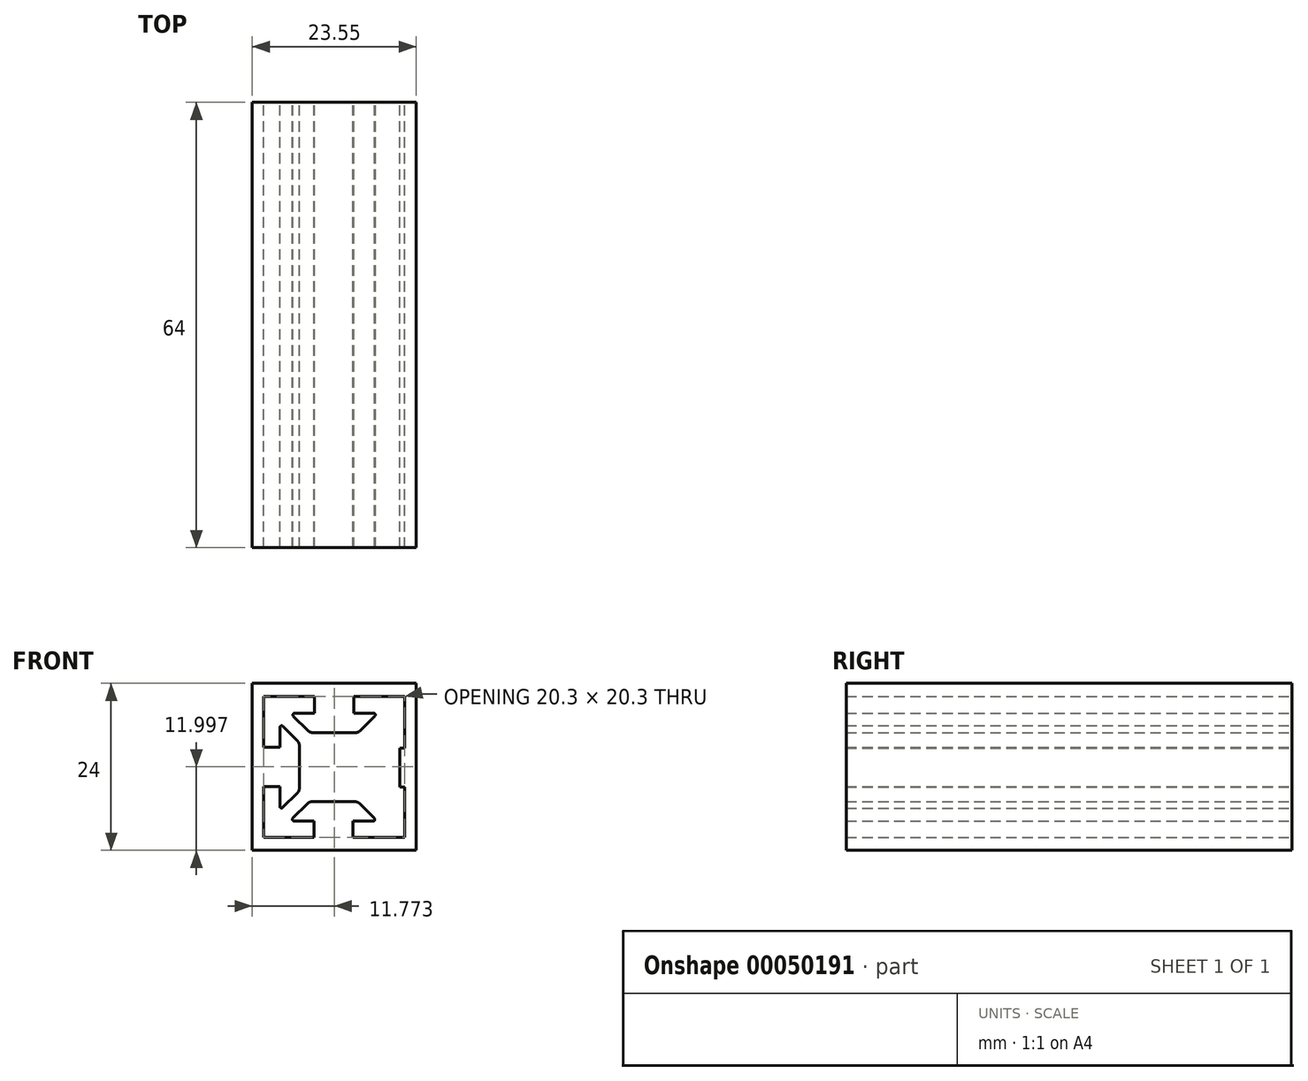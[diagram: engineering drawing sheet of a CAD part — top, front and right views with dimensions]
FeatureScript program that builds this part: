
annotation { "Feature Type Name" : "Feature", "Feature Type Description" : "" }
export const myFeature = defineFeature(function(context is Context, id is Id, definition is map)
    precondition{}
    {
        {
            var Q0;
            Q0=qCreatedBy(makeId("Front.planeOp"),FACE);
            var sketch = newSketch(context, id + "F0", { "sketchPlane" : qUnion([Q0])});
            skLineSegment(sketch, "E0", {"start": v(10.04, -9.96) * mm, "end": v(10.04, -2.96) * mm, "construction": true});
            skLineSegment(sketch, "E1", {"start": v(10.04, 3.04) * mm, "end": v(10.04, 10.04) * mm, "construction": true});
            skLineSegment(sketch, "E2", {"start": v(-6.7, -7.96) * mm, "end": v(-2.7, -3.96) * mm, "construction": true});
            skLineSegment(sketch, "E3", {"start": v(4.04, -2.63) * mm, "end": v(4.04, 2.78) * mm, "construction": true});
            skLineSegment(sketch, "E4", {"start": v(-2.7, -3.96) * mm, "end": v(2.91, -3.96) * mm, "construction": true});
            skLineSegment(sketch, "E5", {"start": v(2.91, -3.96) * mm, "end": v(6.91, -7.96) * mm, "construction": true});
            skLineSegment(sketch, "E6", {"start": v(-2.96, 10.04) * mm, "end": v(-9.96, 10.04) * mm, "construction": true});
            skLineSegment(sketch, "E7", {"start": v(-9.96, 10.04) * mm, "end": v(-9.96, 3.04) * mm, "construction": true});
            skCircle(sketch, "E8", {"center": v(0.04, 0.04) * mm, "radius": 2.1 * mm, "construction": true});
            skLineSegment(sketch, "E9", {"start": v(-7.96, 3.04) * mm, "end": v(-7.96, 6.79) * mm, "construction": true});
            skLineSegment(sketch, "E10", {"start": v(-7.96, 6.79) * mm, "end": v(-3.96, 2.79) * mm, "construction": true});
            skLineSegment(sketch, "E11", {"start": v(-3.96, 2.79) * mm, "end": v(-3.96, -2.71) * mm, "construction": true});
            skLineSegment(sketch, "E12", {"start": v(-3.96, -2.71) * mm, "end": v(-7.96, -6.71) * mm, "construction": true});
            skLineSegment(sketch, "E13", {"start": v(2.9, 4.04) * mm, "end": v(-2.7, 4.04) * mm, "construction": true});
            skLineSegment(sketch, "E14", {"start": v(6.91, -7.96) * mm, "end": v(3.04, -7.96) * mm, "construction": true});
            skLineSegment(sketch, "E15", {"start": v(-7.96, -6.71) * mm, "end": v(-7.96, -2.96) * mm, "construction": true});
            skLineSegment(sketch, "E16", {"start": v(-9.96, -2.96) * mm, "end": v(-9.96, -9.96) * mm, "construction": true});
            skLineSegment(sketch, "E17", {"start": v(-9.96, -9.96) * mm, "end": v(-2.96, -9.96) * mm, "construction": true});
            skLineSegment(sketch, "E18", {"start": v(-2.96, -7.96) * mm, "end": v(-6.7, -7.96) * mm, "construction": true});
            skLineSegment(sketch, "E19", {"start": v(10.04, 10.04) * mm, "end": v(3.04, 10.04) * mm, "construction": true});
            skLineSegment(sketch, "E20", {"start": v(4.04, 2.78) * mm, "end": v(8.04, 6.78) * mm, "construction": true});
            skLineSegment(sketch, "E21", {"start": v(3.04, 8.04) * mm, "end": v(6.91, 8.04) * mm, "construction": true});
            skLineSegment(sketch, "E22", {"start": v(8.04, -2.96) * mm, "end": v(8.04, -6.63) * mm, "construction": true});
            skLineSegment(sketch, "E23", {"start": v(-2.7, 4.04) * mm, "end": v(-6.7, 8.04) * mm, "construction": true});
            skLineSegment(sketch, "E24", {"start": v(8.04, 6.78) * mm, "end": v(8.04, 3.04) * mm, "construction": true});
            skLineSegment(sketch, "E25", {"start": v(6.91, 8.04) * mm, "end": v(2.9, 4.04) * mm, "construction": true});
            skLineSegment(sketch, "E26", {"start": v(8.04, -6.63) * mm, "end": v(4.04, -2.63) * mm, "construction": true});
            skLineSegment(sketch, "E27", {"start": v(-6.7, 8.04) * mm, "end": v(-2.96, 8.04) * mm, "construction": true});
            skLineSegment(sketch, "E28", {"start": v(3.04, -9.96) * mm, "end": v(10.04, -9.96) * mm, "construction": true});
            skLineSegment(sketch, "E29", {"start": v(8.04, 3.04) * mm, "end": v(10.04, 3.04) * mm, "construction": true});
            skLineSegment(sketch, "E30", {"start": v(-2.96, 8.04) * mm, "end": v(-2.96, 10.04) * mm, "construction": true});
            skLineSegment(sketch, "E31", {"start": v(-9.96, 3.04) * mm, "end": v(-7.96, 3.04) * mm, "construction": true});
            skLineSegment(sketch, "E32", {"start": v(3.04, 10.04) * mm, "end": v(3.04, 8.04) * mm, "construction": true});
            skLineSegment(sketch, "E33", {"start": v(10.04, -2.96) * mm, "end": v(8.04, -2.96) * mm, "construction": true});
            skLineSegment(sketch, "E34", {"start": v(-7.96, -2.96) * mm, "end": v(-9.96, -2.96) * mm, "construction": true});
            skLineSegment(sketch, "E35", {"start": v(-2.96, -9.96) * mm, "end": v(-2.96, -7.96) * mm, "construction": true});
            skLineSegment(sketch, "E36", {"start": v(3.04, -7.96) * mm, "end": v(3.04, -9.96) * mm, "construction": true});
            skLineSegment(sketch, "E37.0", {"start": v(-7.33, 5.88) * mm, "end": v(-5.25, 3.8) * mm});
            skLineSegment(sketch, "E38.0", {"start": v(-5.25, -3.72) * mm, "end": v(-7.33, -5.8) * mm});
            skLineSegment(sketch, "E39", {"start": v(-4.96, 3.09) * mm, "end": v(-4.96, -3.02) * mm});
            skLineSegment(sketch, "E40", {"start": v(-7.76, -5.63) * mm, "end": v(-7.76, -2.76) * mm});
            skLineSegment(sketch, "E41", {"start": v(-7.76, 5.7) * mm, "end": v(-7.76, 2.84) * mm});
            skPoint(sketch, "E42.visualSharp", {"position": v(-7.76, 6.3) * mm});
            skArc(sketch, "E42.filletArc", {"start": v(-7.33, 5.88) * mm, "mid": v(-7.6, 5.93) * mm, "end": v(-7.76, 5.7) * mm});
            skPoint(sketch, "E43.visualSharp", {"position": v(-7.76, -6.23) * mm});
            skArc(sketch, "E43.filletArc", {"start": v(-7.76, -5.63) * mm, "mid": v(-7.6, -5.86) * mm, "end": v(-7.33, -5.8) * mm});
            skPoint(sketch, "E44.visualSharp", {"position": v(-4.96, 3.5) * mm});
            skArc(sketch, "E44.filletArc", {"start": v(-4.96, 3.09) * mm, "mid": v(-5.03, 3.47) * mm, "end": v(-5.25, 3.8) * mm});
            skPoint(sketch, "E45.visualSharp", {"position": v(-4.96, -3.43) * mm});
            skArc(sketch, "E45.filletArc", {"start": v(-5.25, -3.72) * mm, "mid": v(-5.03, -3.4) * mm, "end": v(-4.96, -3.02) * mm});
            skLineSegment(sketch, "E46", {"start": v(-7.76, -2.76) * mm, "end": v(-10.1, -2.76) * mm});
            skLineSegment(sketch, "E47", {"start": v(-7.76, 2.84) * mm, "end": v(-10.1, 2.84) * mm});
            skLineSegment(sketch, "E48.1.0", {"start": v(-2.84, -7.76) * mm, "end": v(-2.84, -10.1) * mm});
            skLineSegment(sketch, "E48.1.1", {"start": v(-5.7, -7.76) * mm, "end": v(-2.84, -7.76) * mm});
            skLineSegment(sketch, "E48.1.2", {"start": v(-5.88, -7.33) * mm, "end": v(-3.8, -5.25) * mm});
            skArc(sketch, "E48.1.3", {"start": v(-5.88, -7.33) * mm, "mid": v(-5.93, -7.6) * mm, "end": v(-5.7, -7.76) * mm});
            skArc(sketch, "E48.1.4", {"start": v(-3.09, -4.96) * mm, "mid": v(-3.47, -5.03) * mm, "end": v(-3.8, -5.25) * mm});
            skLineSegment(sketch, "E48.1.5", {"start": v(-3.09, -4.96) * mm, "end": v(3.02, -4.96) * mm});
            skArc(sketch, "E48.1.6", {"start": v(3.72, -5.25) * mm, "mid": v(3.4, -5.03) * mm, "end": v(3.02, -4.96) * mm});
            skLineSegment(sketch, "E48.1.7", {"start": v(3.72, -5.25) * mm, "end": v(5.8, -7.33) * mm});
            skArc(sketch, "E48.1.8", {"start": v(5.63, -7.76) * mm, "mid": v(5.86, -7.6) * mm, "end": v(5.8, -7.33) * mm});
            skLineSegment(sketch, "E48.1.9", {"start": v(5.63, -7.76) * mm, "end": v(2.76, -7.76) * mm});
            skLineSegment(sketch, "E48.1.10", {"start": v(2.76, -7.76) * mm, "end": v(2.76, -10.1) * mm});
            skLineSegment(sketch, "E48.3.1", {"start": v(5.7, 7.76) * mm, "end": v(2.84, 7.76) * mm});
            skLineSegment(sketch, "E48.3.2", {"start": v(5.88, 7.33) * mm, "end": v(3.8, 5.25) * mm});
            skArc(sketch, "E48.3.3", {"start": v(5.88, 7.33) * mm, "mid": v(5.93, 7.6) * mm, "end": v(5.7, 7.76) * mm});
            skArc(sketch, "E48.3.4", {"start": v(3.09, 4.96) * mm, "mid": v(3.47, 5.03) * mm, "end": v(3.8, 5.25) * mm});
            skLineSegment(sketch, "E48.3.5", {"start": v(3.09, 4.96) * mm, "end": v(-3.02, 4.96) * mm});
            skArc(sketch, "E48.3.6", {"start": v(-3.72, 5.25) * mm, "mid": v(-3.4, 5.03) * mm, "end": v(-3.02, 4.96) * mm});
            skLineSegment(sketch, "E48.3.7", {"start": v(-3.72, 5.25) * mm, "end": v(-5.8, 7.33) * mm});
            skArc(sketch, "E48.3.8", {"start": v(-5.63, 7.76) * mm, "mid": v(-5.86, 7.6) * mm, "end": v(-5.8, 7.33) * mm});
            skLineSegment(sketch, "E48.3.9", {"start": v(-5.63, 7.76) * mm, "end": v(-2.76, 7.76) * mm});
            skPoint(sketch, "E48.center", {"position": v(0, 0) * mm});
            skLineSegment(sketch, "E49", {"start": v(-10.1, -2.76) * mm, "end": v(-10.1, -10.1) * mm});
            skLineSegment(sketch, "E50", {"start": v(-10.1, -10.1) * mm, "end": v(-2.84, -10.1) * mm});
            skLineSegment(sketch, "E51", {"start": v(-2.76, 7.76) * mm, "end": v(-2.76, 10.19) * mm});
            skLineSegment(sketch, "E52", {"start": v(2.84, 7.76) * mm, "end": v(2.84, 10.19) * mm});
            skLineSegment(sketch, "E53", {"start": v(-10.1, 2.84) * mm, "end": v(-10.1, 10.19) * mm});
            skLineSegment(sketch, "E54", {"start": v(-10.1, 10.19) * mm, "end": v(-2.76, 10.19) * mm});
            skLineSegment(sketch, "E55", {"start": v(2.84, 10.19) * mm, "end": v(10.2, 10.19) * mm});
            skLineSegment(sketch, "E56", {"start": v(10.2, 10.19) * mm, "end": v(10.2, 2.76) * mm});
            skLineSegment(sketch, "E57", {"start": v(10.2, -2.84) * mm, "end": v(10.2, -10.11) * mm});
            skLineSegment(sketch, "E58", {"start": v(2.76, -10.1) * mm, "end": v(10.2, -10.11) * mm});
            skLineSegment(sketch, "E59.rect.bottom", {"start": v(11.82, -11.96) * mm, "end": v(-11.73, -11.96) * mm});
            skLineSegment(sketch, "E59.rect.top", {"start": v(11.82, 12.04) * mm, "end": v(-11.73, 12.04) * mm});
            skLineSegment(sketch, "E59.rect.left", {"start": v(11.82, -11.96) * mm, "end": v(11.82, 12.04) * mm});
            skLineSegment(sketch, "E59.rect.right", {"start": v(-11.73, -11.96) * mm, "end": v(-11.73, 12.04) * mm});
            skLineSegment(sketch, "E60", {"start": v(10.2, 2.76) * mm, "end": v(9.46, 2.76) * mm});
            skLineSegment(sketch, "E61", {"start": v(9.46, 2.76) * mm, "end": v(9.46, -2.84) * mm});
            skLineSegment(sketch, "E62", {"start": v(9.46, -2.84) * mm, "end": v(10.2, -2.84) * mm});
            skSolve(sketch);
        }
        {
            var Q0;
            Q0=qSketchRegion(id+"F0",true);
            extrude(context, id + "F1", {"entities" : qUnion([Q0]), "depth" : 64 * mm});
        }
    });
